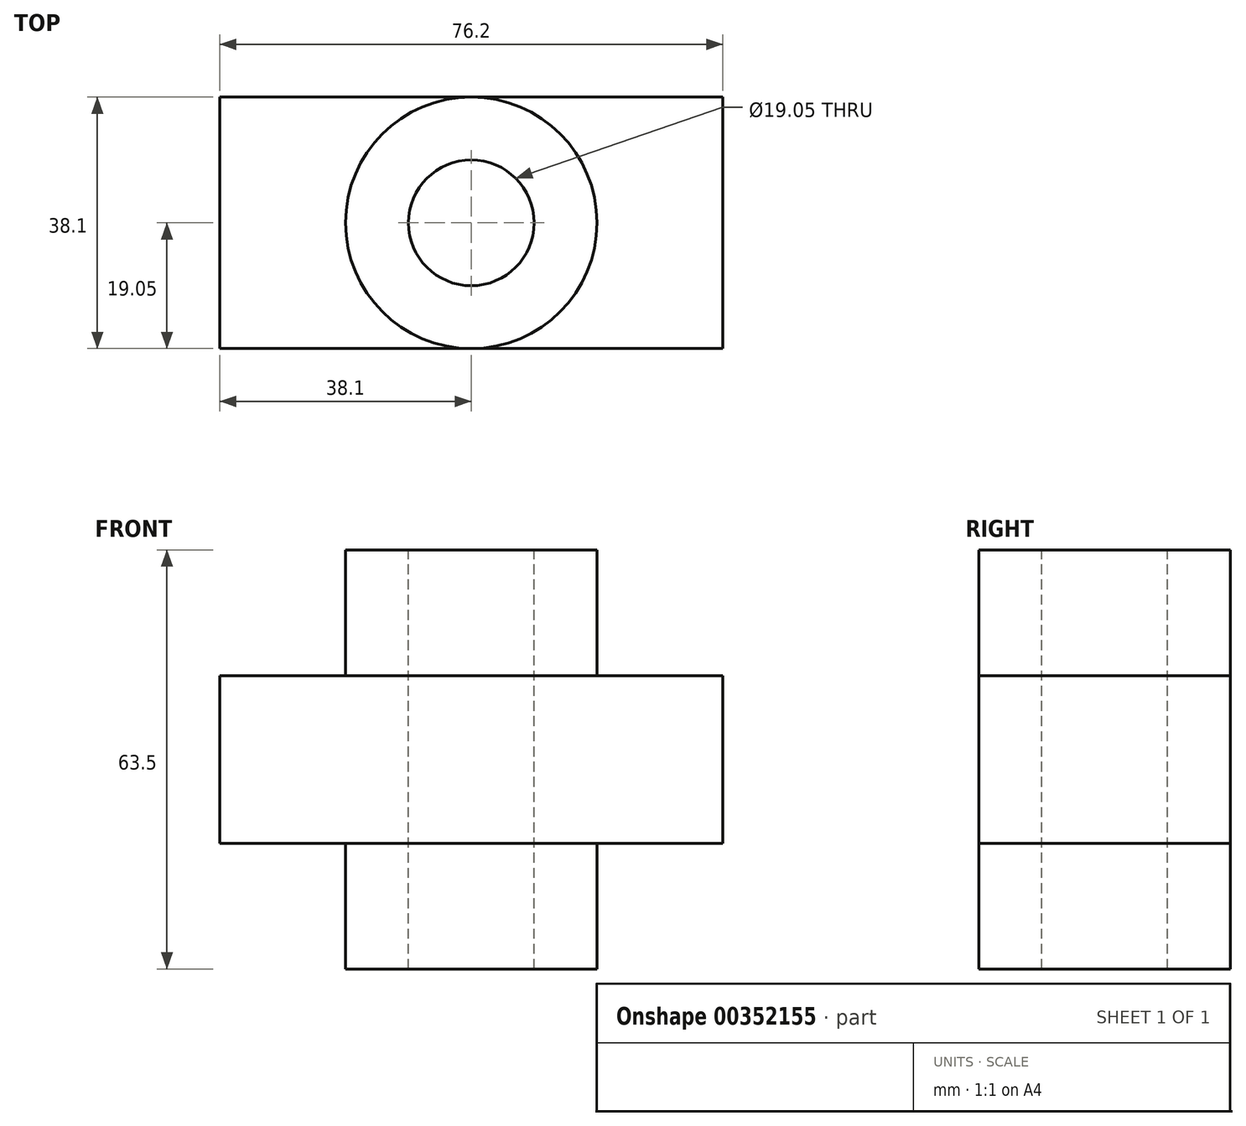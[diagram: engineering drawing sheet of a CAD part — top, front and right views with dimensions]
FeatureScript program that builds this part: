
annotation { "Feature Type Name" : "Feature", "Feature Type Description" : "" }
export const myFeature = defineFeature(function(context is Context, id is Id, definition is map)
    precondition{}
    {
        {
            var Q0;
            Q0=qCreatedBy(makeId("Top.planeOp"),FACE);
            var sketch = newSketch(context, id + "F0", { "sketchPlane" : qUnion([Q0])});
            skLineSegment(sketch, "E0.bottom", {"start": v(0, 0) * mm, "end": v(76.2, 0) * mm});
            skLineSegment(sketch, "E0.top", {"start": v(0, 38.1) * mm, "end": v(76.2, 38.1) * mm});
            skLineSegment(sketch, "E0.left", {"start": v(0, 0) * mm, "end": v(0, 38.1) * mm});
            skLineSegment(sketch, "E0.right", {"start": v(76.2, 0) * mm, "end": v(76.2, 38.1) * mm});
            skSolve(sketch);
        }
        {
            var Q0;
            Q0 = qSketchRegion(id + "F0", true);
            extrude(context, id + "F1", {"entities" : qUnion([Q0]), "depth" : 25.4 * mm});
        }
        {
            var Q0;
            Q0=makeQuery(id+"F1.opExtrude","CAP_FACE",FACE,{"disambiguationData":[OSD([sQuery(id+"F0.wireOp",EDGE,"E0.bottom"),sQuery(id+"F0.wireOp",EDGE,"E0.top"),sQuery(id+"F0.wireOp",EDGE,"E0.left"),sQuery(id+"F0.wireOp",EDGE,"E0.right")])],"isStart":false});
            var sketch = newSketch(context, id + "F2", { "sketchPlane" : qUnion([Q0])});
            skCircle(sketch, "E1", {"center": v(38.1, 19.05) * mm, "radius": 19.05 * mm});
            skSolve(sketch);
        }
        {
            var Q0;
            Q0 = qSketchRegion(id + "F2", true);
            extrude(context, id + "F3", {"entities" : qUnion([Q0]), "operationType" : NewBodyOperationType.ADD, "depth" : 19.05 * mm, "hasSecondDirection" : true, "secondDirectionOppositeDirection" : true, "secondDirectionDepth" : 44.45 * mm});
        }
        {
            var Q0;
            Q0=makeQuery(id+"F3.opExtrude","CAP_FACE",FACE,{"disambiguationData":[OSD([sQuery(id+"F2.wireOp",EDGE,"E1")])],"isStart":false});
            var sketch = newSketch(context, id + "F4", { "sketchPlane" : qUnion([Q0])});
            skCircle(sketch, "E2", {"center": v(38.1, 19.05) * mm, "radius": 9.53 * mm});
            skSolve(sketch);
        }
        {
            var Q0;
            Q0 = qSketchRegion(id + "F4", true);
            extrude(context, id + "F5", {"entities" : qUnion([Q0]), "operationType" : NewBodyOperationType.REMOVE, "endBound" : BoundingType.THROUGH_ALL, "oppositeDirection" : true, "depth" : 25.4 * mm});
        }
    });
